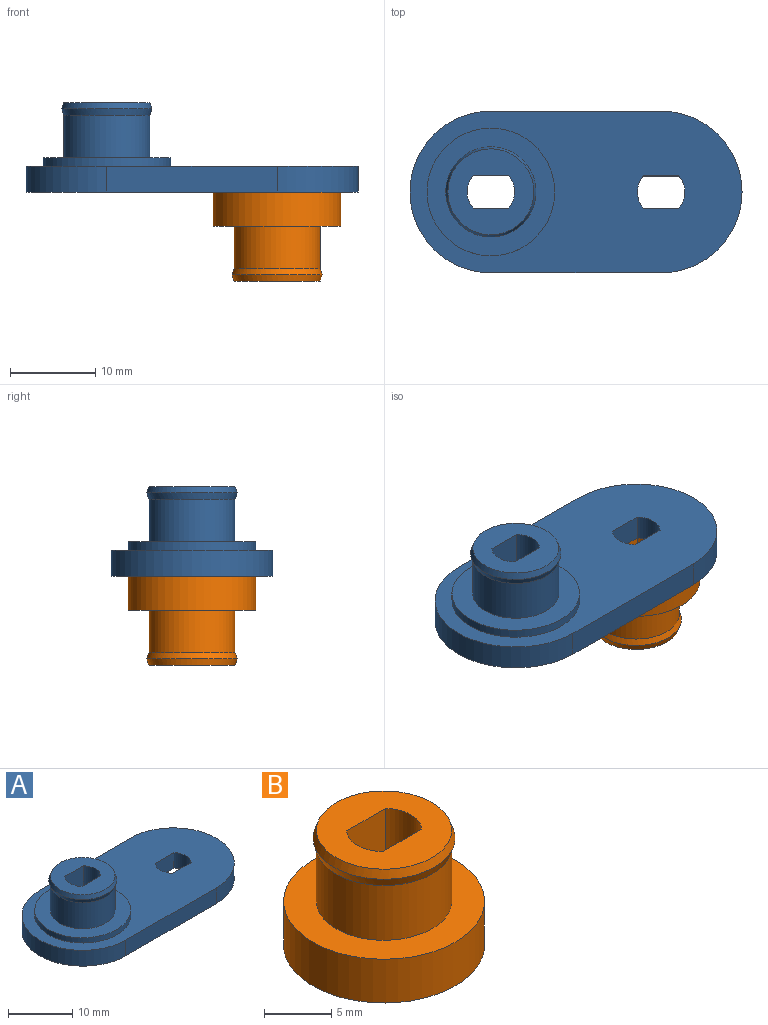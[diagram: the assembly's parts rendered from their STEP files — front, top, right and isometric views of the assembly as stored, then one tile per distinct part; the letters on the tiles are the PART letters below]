
ASSEMBLY  parts=2 mates=1
PART A: 20 faces, bbox 39x19x10.5 mm
  f0: plane 20x3mm, normal (0,1,0), area 60mm2, adj f1,f3,f4,f5
  f1: cylinder r=9.5mm len=19mm, axis (0,0,-1), area 89.5mm2, adj f0,f2,f4,f5
  f2: plane 20x3mm, normal (0,-1,0), area 60mm2, adj f1,f3,f4,f5
  f3: cylinder r=9.5mm len=19mm, axis (0,0,-1), area 89.5mm2, adj f0,f2,f4,f5
  f4: plane 39x19mm, normal (0,0,1), area 467.3mm2, adj f0,f1,f2,f3,f11,f16,f17,f18
  f5: plane 39x19mm, normal (0,0,-1), area 624.5mm2, adj f0,f1,f2,f3,f7,f8,f9,f10
  f6: cylinder r=5.05mm len=10.1mm, axis (0,0,-1), area 158.7mm2, adj f12,f14
  f7: cylinder r=2.8mm len=10.5mm, axis (0,0,-1), area 43.9mm2, adj f5,f8,f10,f13
  f8: plane 10.5x4.11mm, normal (0,-1,0), area 43.2mm2, adj f5,f7,f9,f13
  f9: cylinder r=2.8mm len=10.5mm, axis (0,0,-1), area 43.9mm2, adj f5,f8,f10,f13
  f10: plane 10.5x4.11mm, normal (0,1,0), area 43.2mm2, adj f5,f7,f9,f13
  f11: cylinder r=7.5mm len=15mm, axis (0,0,-1), area 47.1mm2, adj f4,f12
  f12: plane 15x15mm, normal (0,0,1), area 96.6mm2, adj f6,f11
  f13: plane 10.1x10.1mm, normal (0,0,1), area 60.6mm2, adj f7,f8,f9,f10,f15
  f14: cone r=5.3mm half-angle=18.4deg, axis (0,0,1), area 25.7mm2, adj f6,f15
  f15: cone r=5.05mm half-angle=18.4deg, axis (0,0,-1), area 25.7mm2, adj f13,f14
  f16: plane 4.11x3mm, normal (0,-1,0), area 12.3mm2, adj f4,f5,f17,f19
  f17: cylinder r=2.8mm len=3.8mm, axis (0,0,-1), area 12.5mm2, adj f4,f5,f16,f18
  f18: plane 4.11x3mm, normal (0,1,0), area 12.3mm2, adj f4,f5,f17,f19
  f19: cylinder r=2.8mm len=3.8mm, axis (0,0,-1), area 12.5mm2, adj f4,f5,f16,f18
PART B: 11 faces, bbox 15x15x10.5 mm
  f0: plane 15x15mm, normal (0,0,1), area 96.6mm2, adj f4,f7
  f1: cylinder r=2.8mm len=10.5mm, axis (0,0,-1), area 43.9mm2, adj f2,f5,f6,f8
  f2: plane 10.5x4.11mm, normal (0,-1,0), area 43.2mm2, adj f1,f3,f6,f8
  f3: cylinder r=2.8mm len=10.5mm, axis (0,0,-1), area 43.9mm2, adj f2,f5,f6,f8
  f4: cylinder r=7.5mm len=15mm, axis (0,0,-1), area 188.5mm2, adj f0,f6
  f5: plane 10.5x4.11mm, normal (0,1,0), area 43.2mm2, adj f1,f3,f6,f8
  f6: plane 15x15mm, normal (0,0,-1), area 157.2mm2, adj f1,f2,f3,f4,f5
  f7: cylinder r=5.05mm len=10.1mm, axis (0,0,-1), area 158.7mm2, adj f0,f9
  f8: plane 10.1x10.1mm, normal (0,0,1), area 60.6mm2, adj f1,f2,f3,f5,f10
  f9: cone r=5.3mm half-angle=18.4deg, axis (0,0,1), area 25.7mm2, adj f7,f10
  f10: cone r=5.05mm half-angle=18.4deg, axis (0,0,-1), area 25.7mm2, adj f8,f9
PLACE A t=(-9.17,-29.24,0.63)mm
PLACE B rot(axis=(1,0,0),180deg) t=(10.83,-9.24,0.63)mm
MATE fastened A.f3 <-> B.f4  axis (0,0,-1) through (10.83,-9.24,0.63)mm
